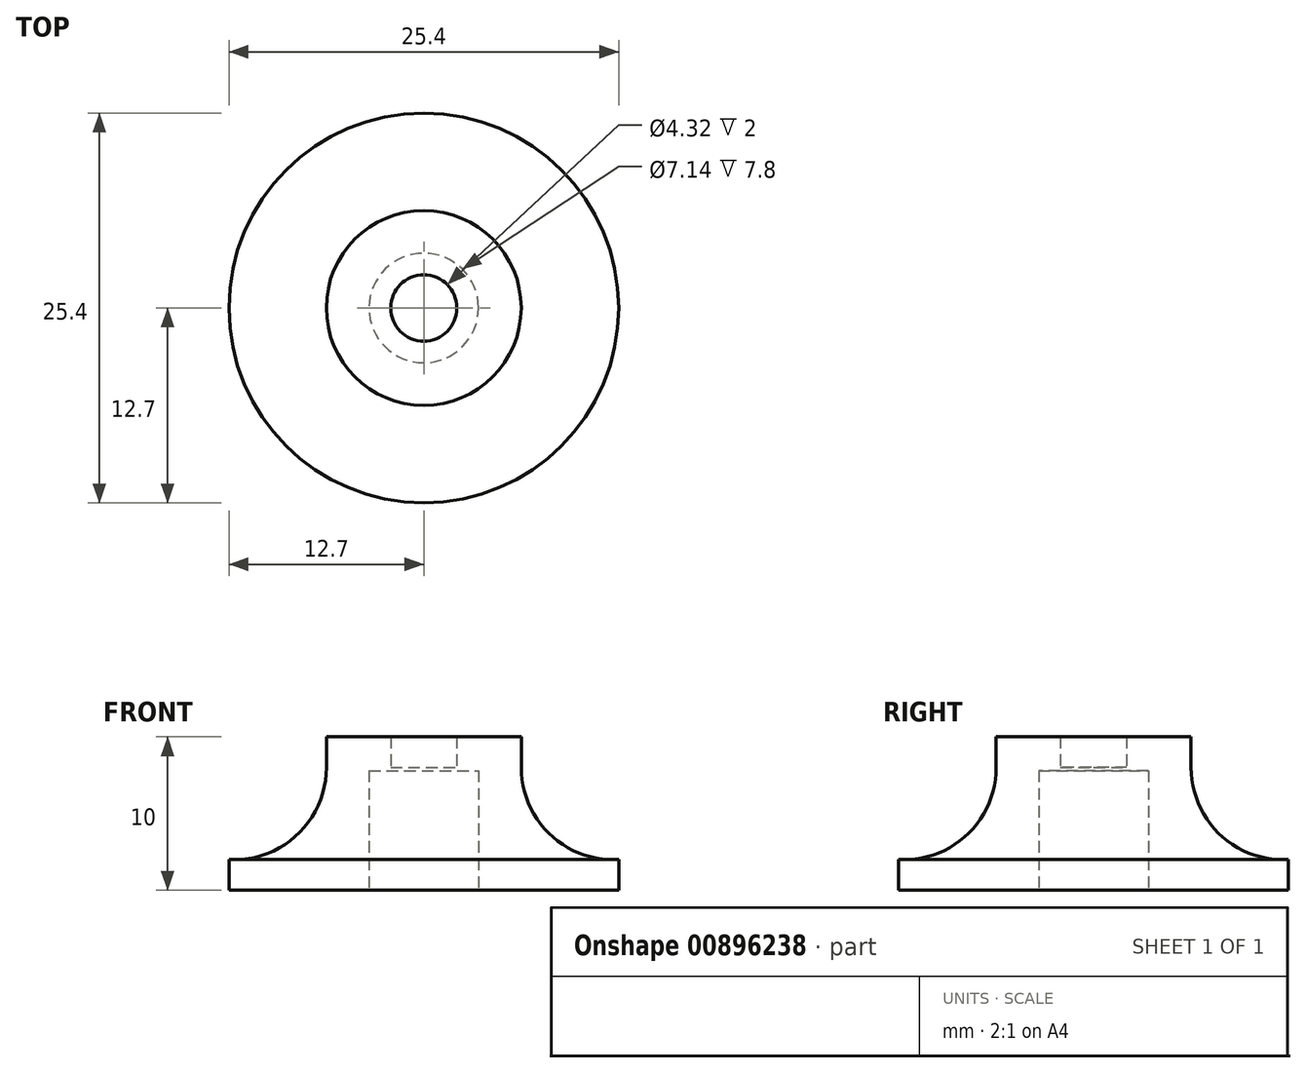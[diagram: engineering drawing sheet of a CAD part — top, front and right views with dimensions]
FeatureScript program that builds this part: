
annotation { "Feature Type Name" : "Feature", "Feature Type Description" : "" }
export const myFeature = defineFeature(function(context is Context, id is Id, definition is map)
    precondition{}
    {
        {
            var Q0;
            Q0=qCreatedBy(makeId("Front.planeOp"),FACE);
            var sketch = newSketch(context, id + "F0", { "sketchPlane" : qUnion([Q0])});
            skLineSegment(sketch, "E0", {"start": v(0, 0) * mm, "end": v(0, 10) * mm});
            skLineSegment(sketch, "E1", {"start": v(0, 10) * mm, "end": v(6.35, 10) * mm});
            skLineSegment(sketch, "E2", {"start": v(6.35, 10) * mm, "end": v(6.35, 8) * mm});
            skLineSegment(sketch, "E3", {"start": v(0, 0) * mm, "end": v(12.7, 0) * mm});
            skLineSegment(sketch, "E4", {"start": v(12.7, 0) * mm, "end": v(12.7, 2) * mm});
            skArc(sketch, "E5", {"start": v(6.35, 8) * mm, "mid": v(8.23, 3.63) * mm, "end": v(12.7, 2) * mm});
            skLineSegment(sketch, "E6", {"start": v(0, 10) * mm, "end": v(2.16, 10) * mm});
            skLineSegment(sketch, "E7", {"start": v(2.16, 10) * mm, "end": v(2.16, 7.8) * mm});
            skLineSegment(sketch, "E8", {"start": v(0, 0) * mm, "end": v(3.57, 0) * mm});
            skLineSegment(sketch, "E9", {"start": v(3.57, 0) * mm, "end": v(3.57, 7.8) * mm});
            skLineSegment(sketch, "E10", {"start": v(2.16, 7.8) * mm, "end": v(3.57, 7.8) * mm});
            skLineSegment(sketch, "E11", {"start": v(2.16, 8) * mm, "end": v(0, 8) * mm});
            skLineSegment(sketch, "E12", {"start": v(2.16, 7.8) * mm, "end": v(0, 7.8) * mm});
            skSolve(sketch);
        }
        {
            var Q0;
            {var subQ3=sQuery(id+"F0.wireOp",EDGE,"E2");Q0=makeQuery(id+"F0.imprint","IMPRINT",FACE,{"disambiguationData":[TD([[makeQuery(id+"F0.imprint","IMPRINT",EDGE,{"derivedFrom":subQ3}),-1.0]])]});}
            var Q1;
            {var subQ0=sQuery(id+"F0.wireOp",EDGE,"E11");Q1=makeQuery(id+"F0.imprint","IMPRINT",FACE,{"disambiguationData":[TD([[makeQuery(id+"F0.imprint","IMPRINT",EDGE,{"derivedFrom":subQ0}),1.0]])]});}
            var Q2;
            Q2=sQuery(id+"F0.wireOp",EDGE,"E0");
            revolve(context, id + "F1", {"surfaceOperationType" : NewSurfaceOperationType.NEW, "entities" : qUnion([Q0, Q1]), "axis" : qUnion([Q2]), "revolveType" : RevolveType.FULL});
        }
    });
